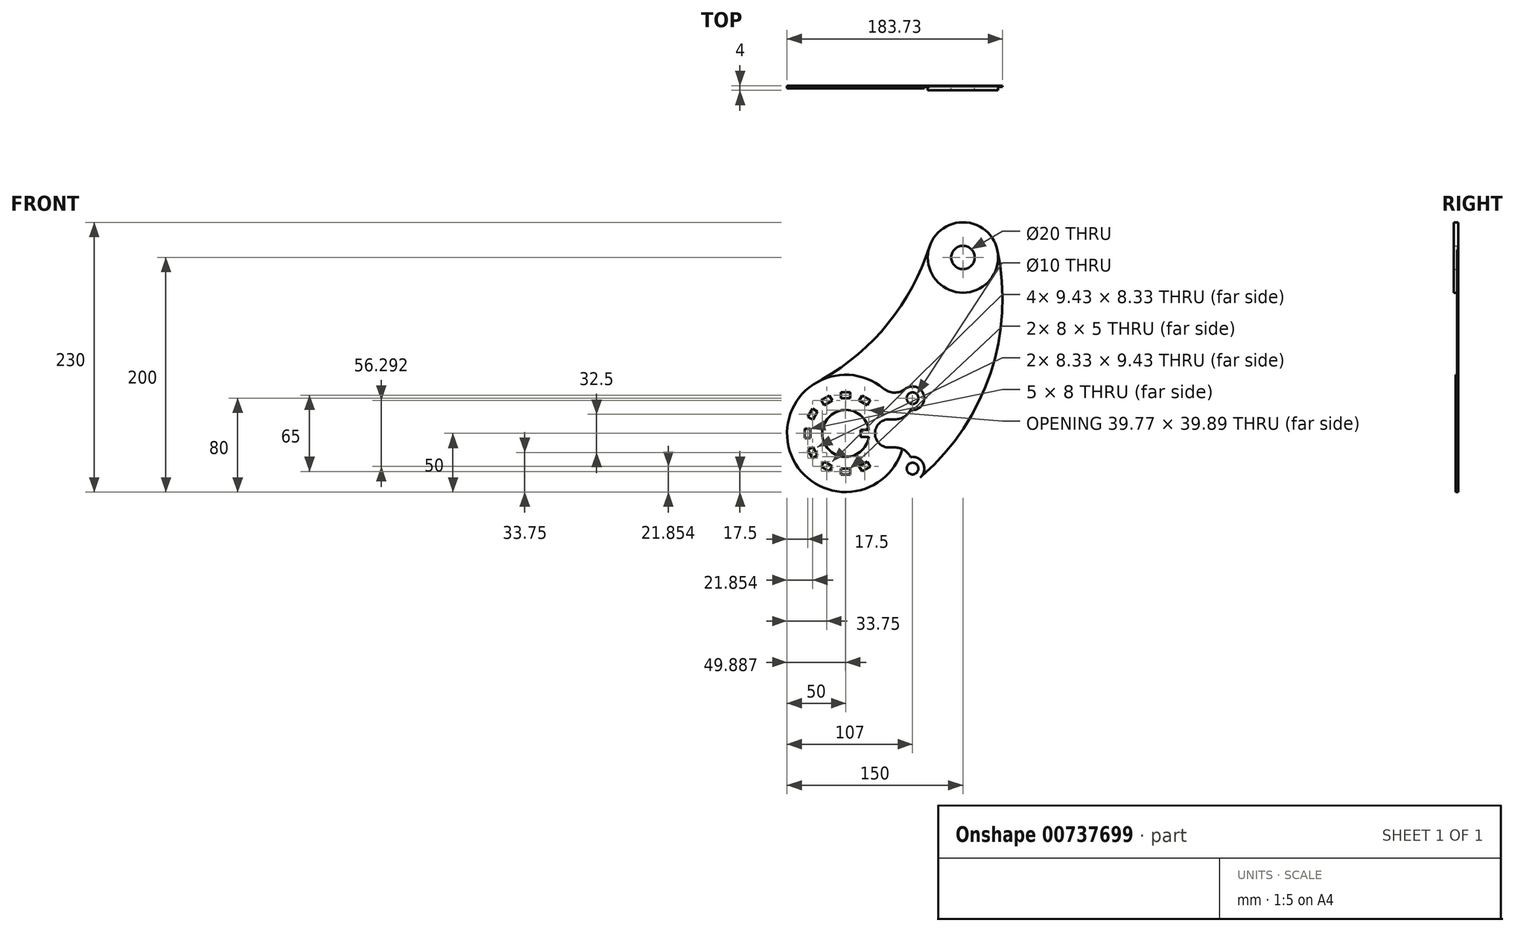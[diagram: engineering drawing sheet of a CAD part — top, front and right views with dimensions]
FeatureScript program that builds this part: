
annotation { "Feature Type Name" : "Feature", "Feature Type Description" : "" }
export const myFeature = defineFeature(function(context is Context, id is Id, definition is map)
    precondition{}
    {
        {
            var Q0;
            Q0=qCreatedBy(makeId("Front.planeOp"),FACE);
            var sketch = newSketch(context, id + "F0", { "sketchPlane" : qUnion([Q0])});
            skCircle(sketch, "E0", {"center": v(0, 0) * mm, "radius": 50 * mm});
            skCircle(sketch, "E1", {"center": v(0, 0) * mm, "radius": 20 * mm});
            skLineSegment(sketch, "E2", {"start": v(19.77, 3) * mm, "end": v(12.77, 3) * mm});
            skLineSegment(sketch, "E3", {"start": v(12.77, 3) * mm, "end": v(12.77, 0) * mm});
            skLineSegment(sketch, "E4.MirrorCS", {"start": v(12.77, -3) * mm, "end": v(12.77, 0) * mm});
            skLineSegment(sketch, "E5.MirrorCS", {"start": v(19.77, -3) * mm, "end": v(12.77, -3) * mm});
            skCircle(sketch, "E6", {"center": v(100, 150) * mm, "radius": 30 * mm});
            skCircle(sketch, "E7", {"center": v(100, 150) * mm, "radius": 10 * mm});
            skCircle(sketch, "E8", {"center": v(57, 30) * mm, "radius": 5 * mm});
            skCircle(sketch, "E9", {"center": v(57, 30) * mm, "radius": 10 * mm});
            skArc(sketch, "E10", {"start": v(37, 12) * mm, "mid": v(25, 0) * mm, "end": v(37, -12) * mm});
            skLineSegment(sketch, "E11", {"start": v(37, 12) * mm, "end": v(42, 12) * mm});
            skLineSegment(sketch, "E12.MirrorCS", {"start": v(37, -12) * mm, "end": v(42, -12) * mm});
            skCircle(sketch, "E13.MirrorC", {"center": v(57, -30) * mm, "radius": 5 * mm});
            skCircle(sketch, "E14.MirrorC", {"center": v(57, -30) * mm, "radius": 10 * mm});
            skArc(sketch, "E15", {"start": v(32.12, 38.32) * mm, "mid": v(41.44, 34.82) * mm, "end": v(50.9, 37.93) * mm});
            skArc(sketch, "E16", {"start": v(42, 12) * mm, "mid": v(49.81, 14.2) * mm, "end": v(55.34, 20.14) * mm});
            skArc(sketch, "E17.MirrorCS", {"start": v(42, -12) * mm, "mid": v(49.81, -14.2) * mm, "end": v(55.34, -20.14) * mm});
            skArc(sketch, "E18.MirrorCS", {"start": v(32.12, -38.32) * mm, "mid": v(41.44, -34.82) * mm, "end": v(50.9, -37.93) * mm});
            skArc(sketch, "E19", {"start": v(-23.83, 43.95) * mm, "mid": v(34.95, 92.3) * mm, "end": v(71.41, 159.1) * mm});
            skArc(sketch, "E20", {"start": v(63.49, -37.6) * mm, "mid": v(123.1, 50.25) * mm, "end": v(129.34, 156.25) * mm});
            skLineSegment(sketch, "E21.bottom", {"start": v(4, 30) * mm, "end": v(-4, 30) * mm});
            skLineSegment(sketch, "E21.top", {"start": v(4, 35) * mm, "end": v(-4, 35) * mm});
            skLineSegment(sketch, "E21.left", {"start": v(4, 30) * mm, "end": v(4, 35) * mm});
            skLineSegment(sketch, "E21.right", {"start": v(-4, 30) * mm, "end": v(-4, 35) * mm});
            skPoint(sketch, "E21.middle", {"position": v(0, 32.5) * mm});
            skLineSegment(sketch, "E22.1.0", {"start": v(-14.04, 32.31) * mm, "end": v(-20.96, 28.31) * mm});
            skLineSegment(sketch, "E22.1.1", {"start": v(-18.46, 23.98) * mm, "end": v(-20.96, 28.31) * mm});
            skLineSegment(sketch, "E22.1.2", {"start": v(-11.54, 27.98) * mm, "end": v(-18.46, 23.98) * mm});
            skLineSegment(sketch, "E22.1.3", {"start": v(-11.54, 27.98) * mm, "end": v(-14.04, 32.31) * mm});
            skLineSegment(sketch, "E22.2.0", {"start": v(-28.31, 20.96) * mm, "end": v(-32.31, 14.04) * mm});
            skLineSegment(sketch, "E22.2.1", {"start": v(-27.98, 11.54) * mm, "end": v(-32.31, 14.04) * mm});
            skLineSegment(sketch, "E22.2.2", {"start": v(-23.98, 18.46) * mm, "end": v(-27.98, 11.54) * mm});
            skLineSegment(sketch, "E22.2.3", {"start": v(-23.98, 18.46) * mm, "end": v(-28.31, 20.96) * mm});
            skLineSegment(sketch, "E22.3.0", {"start": v(-35, 4) * mm, "end": v(-35, -4) * mm});
            skLineSegment(sketch, "E22.3.1", {"start": v(-30, -4) * mm, "end": v(-35, -4) * mm});
            skLineSegment(sketch, "E22.3.2", {"start": v(-30, 4) * mm, "end": v(-30, -4) * mm});
            skLineSegment(sketch, "E22.3.3", {"start": v(-30, 4) * mm, "end": v(-35, 4) * mm});
            skLineSegment(sketch, "E22.4.0", {"start": v(-32.31, -14.04) * mm, "end": v(-28.31, -20.96) * mm});
            skLineSegment(sketch, "E22.4.1", {"start": v(-23.98, -18.46) * mm, "end": v(-28.31, -20.96) * mm});
            skLineSegment(sketch, "E22.4.2", {"start": v(-27.98, -11.54) * mm, "end": v(-23.98, -18.46) * mm});
            skLineSegment(sketch, "E22.4.3", {"start": v(-27.98, -11.54) * mm, "end": v(-32.31, -14.04) * mm});
            skLineSegment(sketch, "E22.5.0", {"start": v(-20.96, -28.31) * mm, "end": v(-14.04, -32.31) * mm});
            skLineSegment(sketch, "E22.5.1", {"start": v(-11.54, -27.98) * mm, "end": v(-14.04, -32.31) * mm});
            skLineSegment(sketch, "E22.5.2", {"start": v(-18.46, -23.98) * mm, "end": v(-11.54, -27.98) * mm});
            skLineSegment(sketch, "E22.5.3", {"start": v(-18.46, -23.98) * mm, "end": v(-20.96, -28.31) * mm});
            skLineSegment(sketch, "E22.6.0", {"start": v(-4, -35) * mm, "end": v(4, -35) * mm});
            skLineSegment(sketch, "E22.6.1", {"start": v(4, -30) * mm, "end": v(4, -35) * mm});
            skLineSegment(sketch, "E22.6.2", {"start": v(-4, -30) * mm, "end": v(4, -30) * mm});
            skLineSegment(sketch, "E22.6.3", {"start": v(-4, -30) * mm, "end": v(-4, -35) * mm});
            skLineSegment(sketch, "E22.7.0", {"start": v(14.04, -32.31) * mm, "end": v(20.96, -28.31) * mm});
            skLineSegment(sketch, "E22.7.1", {"start": v(18.46, -23.98) * mm, "end": v(20.96, -28.31) * mm});
            skLineSegment(sketch, "E22.7.2", {"start": v(11.54, -27.98) * mm, "end": v(18.46, -23.98) * mm});
            skLineSegment(sketch, "E22.7.3", {"start": v(11.54, -27.98) * mm, "end": v(14.04, -32.31) * mm});
            skLineSegment(sketch, "E22.11.0", {"start": v(20.96, 28.31) * mm, "end": v(14.04, 32.31) * mm});
            skLineSegment(sketch, "E22.11.1", {"start": v(11.54, 27.98) * mm, "end": v(14.04, 32.31) * mm});
            skLineSegment(sketch, "E22.11.2", {"start": v(18.46, 23.98) * mm, "end": v(11.54, 27.98) * mm});
            skLineSegment(sketch, "E22.11.3", {"start": v(18.46, 23.98) * mm, "end": v(20.96, 28.31) * mm});
            skSolve(sketch);
        }
        {
            var Q0;
            Q0=makeQuery(id+"F0.imprint","IMPRINT",FACE,{"disambiguationData":[TD([[makeQuery(id+"F0.imprint","IMPRINT",EDGE,{"derivedFrom":sQuery(id+"F0.wireOp",EDGE,"E10")}),-1.0]])]});
            var Q1;
            {var subQ0=sQuery(id+"F0.wireOp",EDGE,"E15");Q1=makeQuery(id+"F0.imprint","IMPRINT",FACE,{"disambiguationData":[TD([[makeQuery(id+"F0.imprint","IMPRINT",EDGE,{"derivedFrom":subQ0}),-1.0]])]});}
            var Q2;
            Q2=makeQuery(id+"F0.imprint","IMPRINT",FACE,{"disambiguationData":[TD([[makeQuery(id+"F0.imprint","IMPRINT",EDGE,{"derivedFrom":sQuery(id+"F0.wireOp",EDGE,"E8")}),-1.0]])]});
            var Q3;
            {var subQ0=sQuery(id+"F0.wireOp",EDGE,"E18.MirrorCS");Q3=makeQuery(id+"F0.imprint","IMPRINT",FACE,{"disambiguationData":[TD([[makeQuery(id+"F0.imprint","IMPRINT",EDGE,{"derivedFrom":subQ0}),1.0]])]});}
            var Q4;
            Q4=makeQuery(id+"F0.imprint","IMPRINT",FACE,{"disambiguationData":[TD([[makeQuery(id+"F0.imprint","IMPRINT",EDGE,{"derivedFrom":sQuery(id+"F0.wireOp",EDGE,"E13.MirrorC")}),1.0]])]});
            var Q5;
            {var subQ0=sQuery(id+"F0.wireOp",EDGE,"E2");Q5=makeQuery(id+"F0.imprint","IMPRINT",FACE,{"disambiguationData":[TD([[makeQuery(id+"F0.imprint","IMPRINT",EDGE,{"derivedFrom":subQ0}),1.0]])]});}
            extrude(context, id + "F1", {"entities" : qUnion([Q0, Q1, Q2, Q3, Q4, Q5]), "depth" : 2.3 * mm, "offsetDistance" : 25 * mm});
        }
        {
            var Q0;
            Q0=makeQuery(id+"F0.imprint","IMPRINT",FACE,{"disambiguationData":[TD([[makeQuery(id+"F0.imprint","IMPRINT",EDGE,{"derivedFrom":sQuery(id+"F0.wireOp",EDGE,"E7")}),-1.0]])]});
            extrude(context, id + "F2", {"entities" : qUnion([Q0]), "depth" : 4 * mm, "offsetDistance" : 25 * mm});
        }
        {
            var Q0;
            {var subQ3=sQuery(id+"F0.wireOp",EDGE,"E15");Q0=makeQuery(id+"F0.imprint","IMPRINT",FACE,{"disambiguationData":[TD([[makeQuery(id+"F0.imprint","IMPRINT",EDGE,{"derivedFrom":subQ3}),1.0]])]});}
            var Q1;
            Q1=makeQuery(id+"F0.imprint","IMPRINT",FACE,{"disambiguationData":[TD([[makeQuery(id+"F0.imprint","IMPRINT",EDGE,{"derivedFrom":sQuery(id+"F0.wireOp",EDGE,"E10")}),1.0]])]});
            extrude(context, id + "F3", {"entities" : qUnion([Q0, Q1]), "depth" : 1.2 * mm, "offsetDistance" : 25 * mm});
        }
        {
            var Q0;
            Q0=makeQuery(id+"F3.opExtrude","CAP_EDGE",EDGE,{"disambiguationData":[OSD([sQuery(id+"F0.wireOp",EDGE,"E16")])],"isStart":false});
            var Q1;
            Q1=makeQuery(id+"F3.opExtrude","CAP_EDGE",EDGE,{"disambiguationData":[OSD([sQuery(id+"F0.wireOp",EDGE,"E11")])],"isStart":false});
            var Q2;
            Q2=makeQuery(id+"F3.opExtrude","CAP_EDGE",EDGE,{"disambiguationData":[OSD([sQuery(id+"F0.wireOp",EDGE,"E10")])],"isStart":false});
            var Q3;
            Q3=makeQuery(id+"F3.opExtrude","CAP_EDGE",EDGE,{"disambiguationData":[OSD([sQuery(id+"F0.wireOp",EDGE,"E9")])],"isStart":false});
            var Q4;
            Q4=makeQuery(id+"F3.opExtrude","CAP_EDGE",EDGE,{"disambiguationData":[OSD([sQuery(id+"F0.wireOp",EDGE,"E17.MirrorCS")])],"isStart":false});
            var Q5;
            Q5=makeQuery(id+"F3.opExtrude","CAP_EDGE",EDGE,{"disambiguationData":[OSD([sQuery(id+"F0.wireOp",EDGE,"E12.MirrorCS")])],"isStart":false});
            var Q6;
            Q6=makeQuery(id+"F3.opExtrude","CAP_EDGE",EDGE,{"disambiguationData":[OSD([sQuery(id+"F0.wireOp",EDGE,"E14.MirrorC")])],"isStart":false});
            var Q7;
            Q7=makeQuery(id+"F3.opExtrude","CAP_EDGE",EDGE,{"disambiguationData":[OSD([sQuery(id+"F0.wireOp",EDGE,"E15")])],"isStart":false});
            var Q8;
            Q8=makeQuery(id+"F3.opExtrude","CAP_EDGE",EDGE,{"disambiguationData":[OSD([sQuery(id+"F0.wireOp",EDGE,"E0")])],"isStart":false});
            fillet(context, id + "F4", {"entities" : qUnion([Q0, Q1, Q2, Q3, Q4, Q5, Q6, Q7, Q8]), "radius" : .25 * mm, "tangentPropagation" : true, "allowEdgeOverflow" : false});
        }
    });
